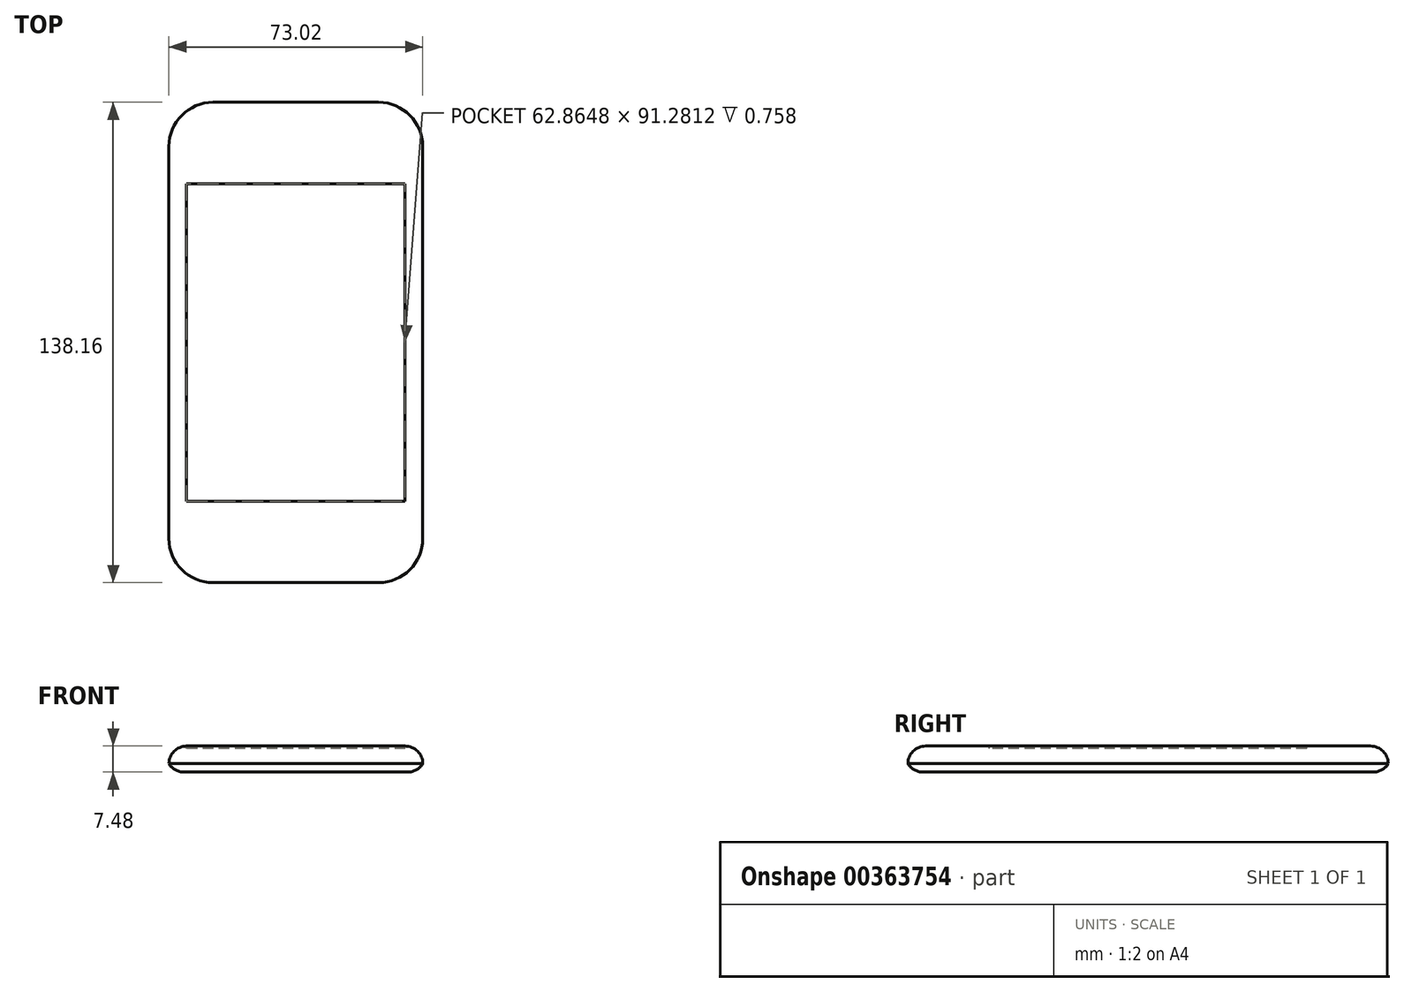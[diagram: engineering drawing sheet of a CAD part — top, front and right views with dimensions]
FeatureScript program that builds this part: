
annotation { "Feature Type Name" : "Feature", "Feature Type Description" : "" }
export const myFeature = defineFeature(function(context is Context, id is Id, definition is map)
    precondition{}
    {
        {
            var Q0;
            Q0=qCreatedBy(makeId("Top.planeOp"),FACE);
            var sketch = newSketch(context, id + "F0", { "sketchPlane" : qUnion([Q0])});
            skLineSegment(sketch, "E0.bottom", {"start": v(23.81, 69.08) * mm, "end": v(-23.81, 69.08) * mm});
            skLineSegment(sketch, "E0.top", {"start": v(23.81, -69.08) * mm, "end": v(-23.81, -69.08) * mm});
            skLineSegment(sketch, "E0.left", {"start": v(36.51, 56.38) * mm, "end": v(36.51, -56.38) * mm});
            skLineSegment(sketch, "E0.right", {"start": v(-36.51, 56.38) * mm, "end": v(-36.51, -56.38) * mm});
            skPoint(sketch, "E0.middle", {"position": v(0, 0) * mm});
            skPoint(sketch, "E1.visualSharp", {"position": v(-36.51, 69.08) * mm});
            skArc(sketch, "E1.filletArc", {"start": v(-23.81, 69.08) * mm, "mid": v(-32.8, 65.36) * mm, "end": v(-36.51, 56.38) * mm});
            skPoint(sketch, "E2.visualSharp", {"position": v(-36.51, -69.08) * mm});
            skArc(sketch, "E2.filletArc", {"start": v(-36.51, -56.38) * mm, "mid": v(-32.8, -65.36) * mm, "end": v(-23.81, -69.08) * mm});
            skPoint(sketch, "E3.visualSharp", {"position": v(36.51, -69.08) * mm});
            skArc(sketch, "E3.filletArc", {"start": v(23.81, -69.08) * mm, "mid": v(32.8, -65.36) * mm, "end": v(36.51, -56.38) * mm});
            skPoint(sketch, "E4.visualSharp", {"position": v(36.51, 69.08) * mm});
            skArc(sketch, "E4.filletArc", {"start": v(36.51, 56.38) * mm, "mid": v(32.8, 65.36) * mm, "end": v(23.81, 69.08) * mm});
            skSolve(sketch);
        }
        {
            var Q0;
            Q0=makeQuery(id+"F0.imprint","IMPRINT",FACE,{"disambiguationData":[TD([[makeQuery(id+"F0.imprint","IMPRINT",EDGE,{"derivedFrom":sQuery(id+"F0.wireOp",EDGE,"E0.bottom")}),1.0]])]});
            extrude(context, id + "F1", {"entities" : qUnion([Q0]), "depth" : 7.48 * mm});
        }
        {
            var Q0;
            Q0=makeQuery(id+"F1.opExtrude","CAP_EDGE",EDGE,{"disambiguationData":[OSD([sQuery(id+"F0.wireOp",EDGE,"E0.top")])],"isStart":false});
            fillet(context, id + "F2", {"entities" : qUnion([Q0]), "radius" : 5.08 * mm, "tangentPropagation" : true, "allowEdgeOverflow" : false});
        }
        {
            var Q0;
            Q0=makeQuery(id+"F1.opExtrude","CAP_EDGE",EDGE,{"disambiguationData":[OSD([sQuery(id+"F0.wireOp",EDGE,"E0.top")])],"isStart":true});
            fillet(context, id + "F3", {"entities" : qUnion([Q0]), "radius" : 5.08 * mm, "tangentPropagation" : true, "allowEdgeOverflow" : false});
        }
        {
            var Q0;
            Q0=makeQuery(id+"F1.opExtrude","CAP_FACE",FACE,{"disambiguationData":[OSD([sQuery(id+"F0.wireOp",EDGE,"E0.bottom"),sQuery(id+"F0.wireOp",EDGE,"E0.top"),sQuery(id+"F0.wireOp",EDGE,"E0.left"),sQuery(id+"F0.wireOp",EDGE,"E0.right"),sQuery(id+"F0.wireOp",EDGE,"E1.filletArc"),sQuery(id+"F0.wireOp",EDGE,"E2.filletArc"),sQuery(id+"F0.wireOp",EDGE,"E3.filletArc"),sQuery(id+"F0.wireOp",EDGE,"E4.filletArc")])],"isStart":false});
            var sketch = newSketch(context, id + "F4", { "sketchPlane" : qUnion([Q0])});
            skLineSegment(sketch, "E5.bottom", {"start": v(31.43, 45.64) * mm, "end": v(-31.43, 45.64) * mm});
            skLineSegment(sketch, "E5.top", {"start": v(31.43, -45.64) * mm, "end": v(-31.43, -45.64) * mm});
            skLineSegment(sketch, "E5.left", {"start": v(31.43, 45.64) * mm, "end": v(31.43, -45.64) * mm});
            skLineSegment(sketch, "E5.right", {"start": v(-31.43, 45.64) * mm, "end": v(-31.43, -45.64) * mm});
            skPoint(sketch, "E5.middle", {"position": v(0, 0) * mm});
            skSolve(sketch);
        }
        {
            var Q0;
            Q0=makeQuery(id+"F4.imprint","IMPRINT",FACE,{"disambiguationData":[TD([[makeQuery(id+"F4.imprint","IMPRINT",EDGE,{"derivedFrom":sQuery(id+"F4.wireOp",EDGE,"E5.bottom")}),1.0]])]});
            extrude(context, id + "F5", {"entities" : qUnion([Q0]), "operationType" : NewBodyOperationType.REMOVE, "oppositeDirection" : true, "depth" : 0.76 * mm});
        }
    });
